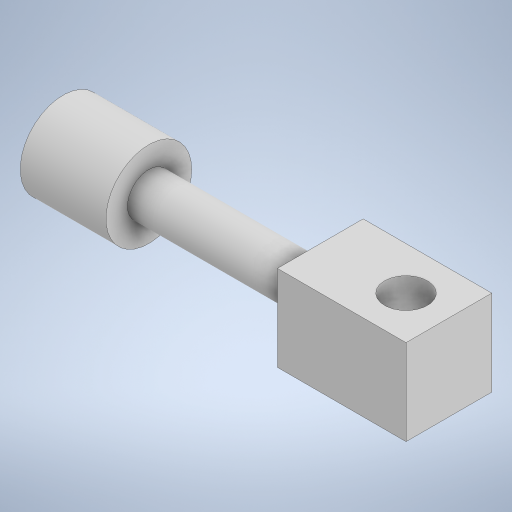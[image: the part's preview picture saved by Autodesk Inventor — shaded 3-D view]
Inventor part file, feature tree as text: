
AUTODESK INVENTOR PART (.ipt)
format: ipt  version: 2023 (Build 270158000, 158)  size: 257,024 bytes
history: native  units: in
note: dims shown in document units (in); Inventor stores cm internally (conversion verified against a paired STEP export)
features: extrude x1, plane x1, revolve x1, sketch x1
ambient origin geometry x8: Origin, YZ Plane, XZ Plane, XY Plane, X Axis, Y Axis, Z Axis, Center Point
bodies: Solid1 (feature_tree)
feature tree (4):
  extrude  "Extrusion1"  Depth=0.5in TaperAngle=0.0deg
  plane  "Work Plane2"
  revolve  "Revolution2"  [1 undecoded]
  sketch  "Sketch4"  dims[d6=0.0in d12=0.5in d13=0.0in d15=0.25in d16=0.25in d17=0.5in d18=0.75in d19=0.25in d20=1.0in d21=0.125in d22=0.25in d23=0.5in d24=360.0deg]
note: 1 required parameter value undecoded (feature->parameter linkage not recoverable at this tier; creation-order binding heuristic only, values carry confidence <= 0.55)
